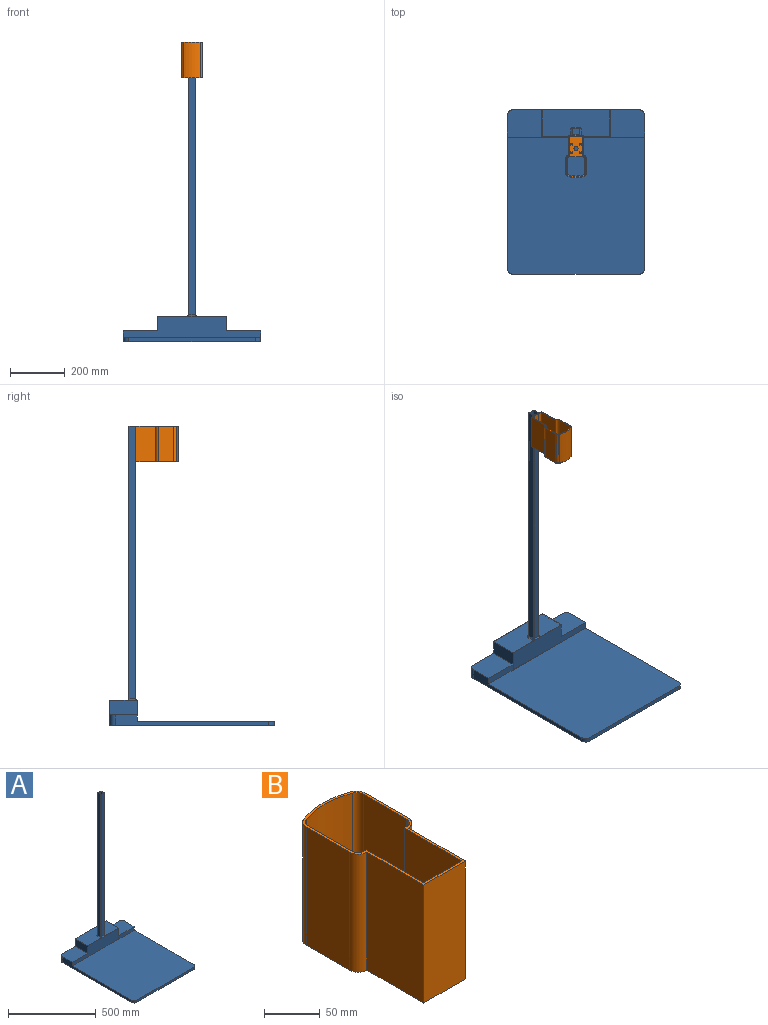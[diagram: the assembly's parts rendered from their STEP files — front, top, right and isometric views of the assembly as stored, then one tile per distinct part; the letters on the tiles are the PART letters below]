
ASSEMBLY  parts=2 mates=2
PART A: 52 faces, bbox 500x600x1092.5 mm
  f0: plane 1050x23mm, normal (0,-1,0), area 24150mm2, adj f16,f18,f42,f51
  f1: plane 460x92.5mm, normal (0,1,0), area 13150mm2, adj f2,f3,f4,f5,f19,f21,f22,f28
  f2: plane 245x97.5mm, normal (0,0,-1), area 23161.9mm2, adj f1,f4,f5,f6,f7,f8,f9,f10
  f3: plane 245x97.5mm, normal (0,0,1), area 23887.5mm2, adj f1,f4,f5,f6
  f4: plane 97.5x75mm, normal (-1,0,0), area 7312.5mm2, adj f1,f2,f3,f6
  f5: plane 97.5x75mm, normal (1,0,0), area 7312.5mm2, adj f1,f2,f3,f6
  f6: plane 245x75mm, normal (0,1,0), area 18375mm2, adj f2,f3,f4,f5
  f7: cylinder r=2mm len=72.5mm, axis (0,0,-1), area 227.8mm2, adj f2,f8,f14,f15
  f8: plane 72.5x23mm, normal (-1,0,0), area 1667.5mm2, adj f2,f7,f9,f15
  f9: cylinder r=2mm len=72.5mm, axis (0,0,-1), area 227.8mm2, adj f2,f8,f10,f15,f16
  f10: plane 47.5x23mm, normal (0,1,0), area 1092.5mm2, adj f2,f9,f11,f51
  f11: cylinder r=2mm len=72.5mm, axis (0,0,-1), area 227.8mm2, adj f2,f10,f12,f15,f18
  f12: plane 72.5x23mm, normal (1,0,0), area 1667.5mm2, adj f2,f11,f13,f15
  f13: cylinder r=2mm len=72.5mm, axis (0,0,-1), area 227.8mm2, adj f2,f12,f14,f15
  f14: plane 72.5x23mm, normal (0,-1,0), area 1667.5mm2, adj f2,f7,f13,f15
  f15: plane 27x27mm, normal (0,0,-1), area 150.6mm2, adj f7,f8,f9,f11,f12,f13,f14,f16
  f16: plane 1075x25mm, normal (1,0,0), area 24775mm2, adj f0,f9,f15,f17,f42,f51
  f17: plane 1075x23mm, normal (0,1,0), area 24725mm2, adj f15,f16,f18,f42
  f18: plane 1075x25mm, normal (-1,0,0), area 24775mm2, adj f0,f11,f15,f17,f42,f51
  f19: plane 125x100mm, normal (0,0,1), area 12414.2mm2, adj f1,f20,f21,f29,f32
  f20: plane 560x40mm, normal (1,0,0), area 10400mm2, adj f19,f21,f26,f27,f28,f29
  f21: cylinder r=20mm len=40mm, axis (0,0,-1), area 1256.6mm2, adj f1,f19,f20,f28
  f22: cylinder r=20mm len=40mm, axis (0,0,-1), area 1256.6mm2, adj f1,f23,f28,f30
  f23: plane 560x40mm, normal (-1,0,0), area 10400mm2, adj f22,f24,f27,f28,f29,f30
  f24: cylinder r=20mm len=20mm, axis (0,0,-1), area 471.2mm2, adj f23,f25,f27,f28
  f25: plane 460x15mm, normal (0,-1,0), area 6900mm2, adj f24,f26,f27,f28
  f26: cylinder r=20mm len=20mm, axis (0,0,-1), area 471.2mm2, adj f20,f25,f27,f28
  f27: plane 500x500mm, normal (0,0,1), area 249828.3mm2, adj f20,f23,f24,f25,f26,f29
  f28: plane 600x500mm, normal (0,0,-1), area 299656.6mm2, adj f1,f20,f21,f22,f23,f24,f25,f26
  f29: plane 500x77.5mm, normal (0,-1,0), area 25625mm2, adj f19,f20,f23,f27,f30,f31,f32,f33
  f30: plane 125x100mm, normal (0,0,1), area 12414.2mm2, adj f1,f22,f23,f29,f31
  f31: plane 100x52.5mm, normal (-1,0,0), area 5250mm2, adj f1,f29,f30,f33
  f32: plane 100x52.5mm, normal (1,0,0), area 5250mm2, adj f1,f19,f29,f33
  f33: plane 250x100mm, normal (0,0,1), area 23673.1mm2, adj f1,f29,f31,f32,f43,f44,f45,f47
  f34: plane 995x23mm, normal (0,-1,0), area 22885mm2, adj f35,f41,f42,f46
  f35: cylinder r=2mm len=995mm, axis (0,0,-1), area 3125.9mm2, adj f34,f36,f42,f44
  f36: plane 995x23mm, normal (1,0,0), area 22885mm2, adj f35,f37,f42,f43
  f37: cylinder r=2mm len=995mm, axis (0,0,-1), area 3125.9mm2, adj f36,f38,f42,f45
  f38: plane 995x23mm, normal (0,1,0), area 22885mm2, adj f37,f39,f42,f47
  f39: cylinder r=2mm len=995mm, axis (0,0,-1), area 3125.9mm2, adj f38,f40,f42,f49
  f40: plane 995x23mm, normal (-1,0,0), area 22885mm2, adj f39,f41,f42,f50
  f41: cylinder r=2mm len=995mm, axis (0,0,-1), area 3125.9mm2, adj f34,f40,f42,f48
  f42: plane 27x27mm, normal (0,0,1), area 196.6mm2, adj f0,f16,f17,f18,f34,f35,f36,f37
  f43: cylinder r=5mm len=23mm, axis (0,-1,0), area 180.6mm2, adj f33,f36,f44,f45
  f44: torus R=7mm, axis (0,0,1), area 47.1mm2, adj f33,f35,f43,f46
  f45: torus R=7mm, axis (0,0,1), area 47.1mm2, adj f33,f37,f43,f47
  f46: cylinder r=5mm len=23mm, axis (-1,0,0), area 180.6mm2, adj f29,f34,f44,f48
  f47: cylinder r=5mm len=23mm, axis (1,0,0), area 180.6mm2, adj f33,f38,f45,f49
  f48: torus R=7mm, axis (0,0,1), area 47.1mm2, adj f33,f41,f46,f50
  f49: torus R=7mm, axis (0,0,1), area 47.1mm2, adj f33,f39,f47,f50
  f50: cylinder r=5mm len=23mm, axis (0,1,0), area 180.6mm2, adj f33,f40,f48,f49
  f51: plane 23x2mm, normal (0,0,-1), area 46mm2, adj f0,f10,f16,f18
PART B: 62 faces, bbox 75x154.5x130 mm
  f0: plane 149.5x70mm, normal (0,0,1), area 3992.9mm2, adj f1,f2,f3,f4,f5,f6,f7,f17
  f1: cylinder r=5mm len=4.67mm, axis (0,0,-1), area 15.1mm2, adj f0,f2,f23,f24
  f2: cylinder r=79mm len=56.58mm, axis (0,0,-1), area 144.7mm2, adj f0,f1,f3,f24
  f3: cylinder r=5mm len=4.67mm, axis (0,0,-1), area 15.1mm2, adj f0,f2,f4,f24
  f4: plane 55.09x2.5mm, normal (-1,0,0), area 137.7mm2, adj f0,f3,f5,f24
  f5: cylinder r=5mm len=5mm, axis (0,0,-1), area 19.6mm2, adj f0,f4,f6,f24
  f6: plane 53x2.5mm, normal (0,1,0), area 132.5mm2, adj f0,f5,f7,f24
  f7: cylinder r=5mm len=5mm, axis (0,0,-1), area 19.6mm2, adj f0,f6,f23,f24
  f8: cylinder r=11mm len=130mm, axis (0,0,-1), area 2246.2mm2, adj f9,f22,f24,f37
  f9: plane 130x72.5mm, normal (-1,0,0), area 9425mm2, adj f8,f10,f24,f37
  f10: plane 130x53mm, normal (0,-1,0), area 6890mm2, adj f9,f11,f24,f37
  f11: plane 130x72.5mm, normal (1,0,0), area 9425mm2, adj f10,f12,f24,f37
  f12: cylinder r=11mm len=130mm, axis (0,0,-1), area 2246.2mm2, adj f11,f13,f24,f37
  f13: plane 130x55.09mm, normal (1,0,0), area 7162mm2, adj f12,f14,f24,f37
  f14: cylinder r=11mm len=130mm, axis (0,0,-1), area 1722.5mm2, adj f13,f15,f24,f37
  f15: cylinder r=85mm len=130mm, axis (0,0,-1), area 8093.9mm2, adj f14,f16,f24,f37
  f16: cylinder r=11mm len=130mm, axis (0,0,-1), area 1722.5mm2, adj f15,f22,f24,f37
  f17: cylinder r=7.5mm len=15mm, axis (0,0,-1), area 117.8mm2, adj f0,f24
  f18: cylinder r=1.25mm len=10mm, axis (0,0,-1), area 78.5mm2, adj f24,f43
  f19: cylinder r=1.25mm len=10mm, axis (0,0,-1), area 78.5mm2, adj f24,f49
  f20: cylinder r=1.25mm len=10mm, axis (0,0,-1), area 78.5mm2, adj f24,f61
  f21: cylinder r=1.25mm len=10mm, axis (0,0,-1), area 78.5mm2, adj f24,f55
  f22: plane 130x55.09mm, normal (-1,0,0), area 7162mm2, adj f8,f16,f24,f37
  f23: plane 55.09x2.5mm, normal (1,0,0), area 137.7mm2, adj f0,f1,f7,f24
  f24: plane 154.5x75mm, normal (0,0,-1), area 5252.1mm2, adj f1,f2,f3,f4,f5,f6,f7,f8
  f25: plane 127.5x2.5mm, normal (0,1,0), area 318.7mm2, adj f0,f26,f36,f37
  f26: cylinder r=8.5mm len=127.5mm, axis (0,0,-1), area 1702.4mm2, adj f0,f25,f27,f37
  f27: plane 127.5x55.09mm, normal (1,0,0), area 7024.3mm2, adj f0,f26,f28,f37
  f28: cylinder r=8.5mm len=127.5mm, axis (0,0,-1), area 1305.4mm2, adj f0,f27,f29,f37
  f29: cylinder r=82.5mm len=127.5mm, axis (0,0,-1), area 7704.8mm2, adj f0,f28,f30,f37
  f30: cylinder r=8.5mm len=127.5mm, axis (0,0,-1), area 1305.4mm2, adj f0,f29,f31,f37
  f31: plane 127.5x55.09mm, normal (-1,0,0), area 7024.3mm2, adj f0,f30,f32,f37
  f32: cylinder r=8.5mm len=127.5mm, axis (0,0,-1), area 1702.4mm2, adj f0,f31,f33,f37
  f33: plane 127.5x2.5mm, normal (0,1,0), area 318.7mm2, adj f0,f32,f34,f37
  f34: plane 127.5x72.5mm, normal (-1,0,0), area 9243.8mm2, adj f0,f33,f35,f37
  f35: plane 127.5x48mm, normal (0,1,0), area 6120mm2, adj f0,f34,f36,f37
  f36: plane 127.5x72.5mm, normal (1,0,0), area 9243.8mm2, adj f0,f25,f35,f37
  f37: plane 154.5x75mm, normal (0,0,1), area 1059.1mm2, adj f8,f9,f10,f11,f12,f13,f14,f15
  f38: plane 7.5x5mm, normal (1,0,0), area 37.5mm2, adj f0,f39,f42,f43
  f39: plane 7.5x7.5mm, normal (0,1,0), area 56.2mm2, adj f0,f38,f40,f43
  f40: plane 7.5x7.5mm, normal (-1,0,0), area 56.3mm2, adj f0,f39,f41,f43
  f41: plane 7.5x5mm, normal (0,-1,0), area 37.5mm2, adj f0,f40,f42,f43
  f42: cylinder r=2.5mm len=7.5mm, axis (0,0,-1), area 29.5mm2, adj f0,f38,f41,f43
  f43: plane 7.5x7.5mm, normal (0,0,1), area 50mm2, adj f18,f38,f39,f40,f41,f42
  f44: plane 7.5x7.5mm, normal (1,0,0), area 56.3mm2, adj f0,f45,f48,f49
  f45: plane 7.5x7.5mm, normal (0,1,0), area 56.2mm2, adj f0,f44,f46,f49
  f46: plane 7.5x5mm, normal (-1,0,0), area 37.5mm2, adj f0,f45,f47,f49
  f47: cylinder r=2.5mm len=7.5mm, axis (0,0,-1), area 29.5mm2, adj f0,f46,f48,f49
  f48: plane 7.5x5mm, normal (0,-1,0), area 37.5mm2, adj f0,f44,f47,f49
  f49: plane 7.5x7.5mm, normal (0,0,1), area 50mm2, adj f19,f44,f45,f46,f47,f48
  f50: plane 7.5x7.5mm, normal (0,-1,0), area 56.2mm2, adj f0,f51,f54,f55
  f51: plane 7.5x5mm, normal (1,0,0), area 37.5mm2, adj f0,f50,f52,f55
  f52: cylinder r=2.5mm len=7.5mm, axis (0,0,-1), area 29.5mm2, adj f0,f51,f53,f55
  f53: plane 7.5x5mm, normal (0,1,0), area 37.5mm2, adj f0,f52,f54,f55
  f54: plane 7.5x7.5mm, normal (-1,0,0), area 56.2mm2, adj f0,f50,f53,f55
  f55: plane 7.5x7.5mm, normal (0,0,1), area 50mm2, adj f21,f50,f51,f52,f53,f54
  f56: plane 7.5x7.5mm, normal (0,-1,0), area 56.2mm2, adj f0,f57,f60,f61
  f57: plane 7.5x7.5mm, normal (1,0,0), area 56.2mm2, adj f0,f56,f58,f61
  f58: plane 7.5x5mm, normal (0,1,0), area 37.5mm2, adj f0,f57,f59,f61
  f59: cylinder r=2.5mm len=7.5mm, axis (0,0,-1), area 29.5mm2, adj f0,f58,f60,f61
  f60: plane 7.5x5mm, normal (-1,0,0), area 37.5mm2, adj f0,f56,f59,f61
  f61: plane 7.5x7.5mm, normal (0,0,1), area 50mm2, adj f20,f56,f57,f58,f59,f60
PLACE A t=(-65.21,67.74,-65.74)mm
PLACE B rot(axis=(0,0,1),180deg) t=(-65.21,203.24,896.76)mm
MATE fastened B.f10 <-> A.f34  axis (0,1,0) through (-65.21,272.74,1026.76)mm
MATE fastened A.f28 <-> A.f28  axis (0,0,-1) through (-315.21,347.74,-65.74)mm
